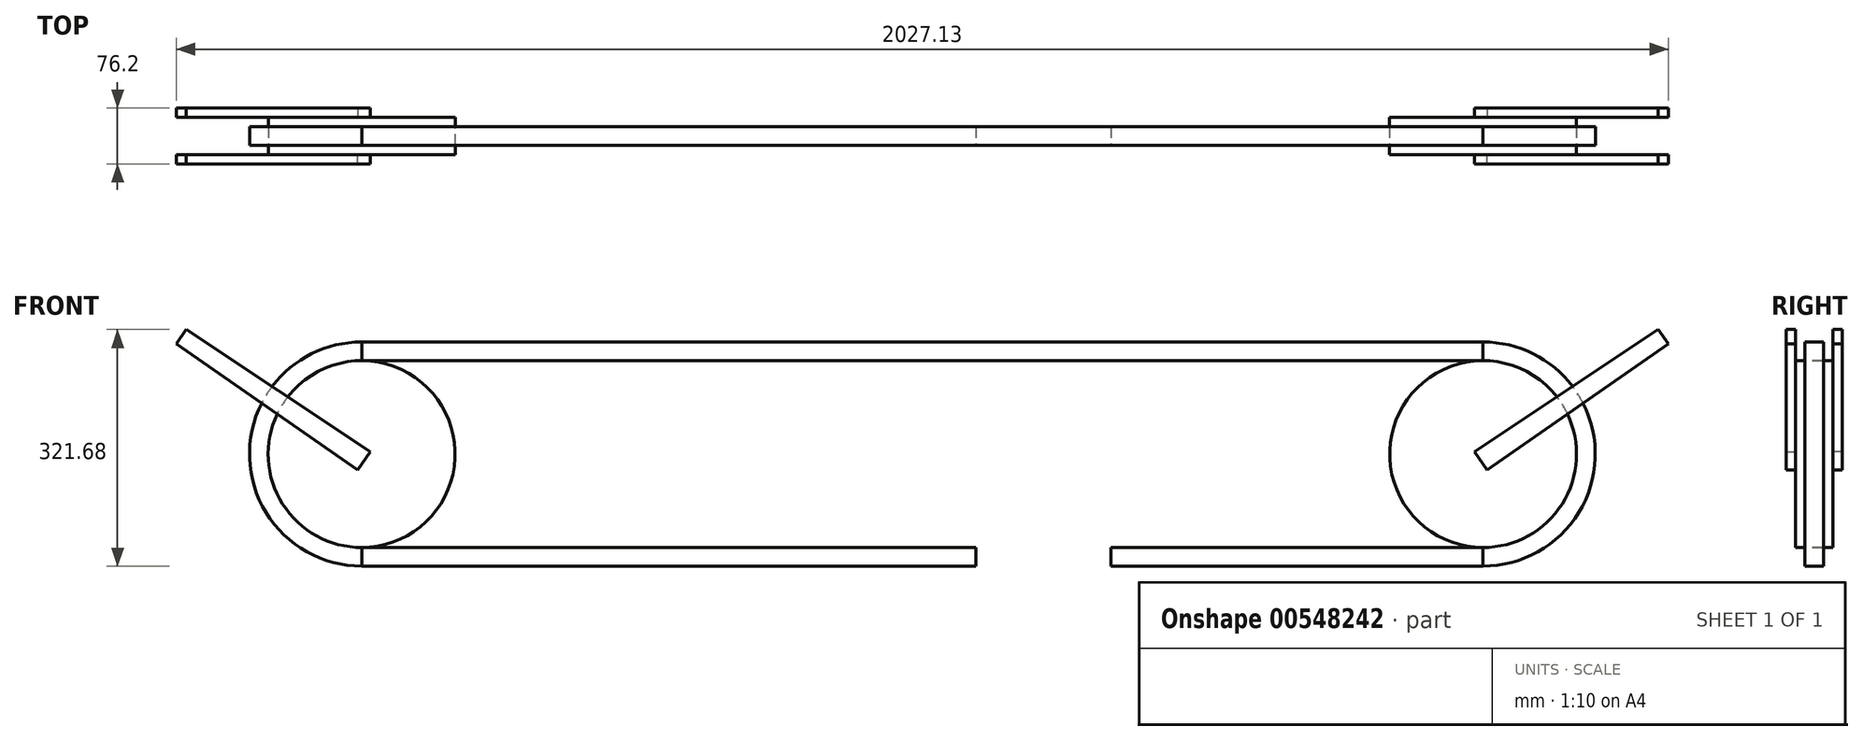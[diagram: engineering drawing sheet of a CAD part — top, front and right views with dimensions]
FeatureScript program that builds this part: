
annotation { "Feature Type Name" : "Feature", "Feature Type Description" : "" }
export const myFeature = defineFeature(function(context is Context, id is Id, definition is map)
    precondition{}
    {
        {
            var Q0;
            Q0=qCreatedBy(makeId("Front.planeOp"),FACE);
            var sketch = newSketch(context, id + "F0", { "sketchPlane" : qUnion([Q0])});
            skLineSegment(sketch, "E0", {"start": v(0, 0) * mm, "end": v(183.8, 0) * mm, "construction": true});
            skLineSegment(sketch, "E1.bottom", {"start": v(0, 0) * mm, "end": v(-834.53, 0) * mm});
            skLineSegment(sketch, "E1.top", {"start": v(0, -25.4) * mm, "end": v(-834.53, -25.4) * mm});
            skLineSegment(sketch, "E1.left", {"start": v(0, 0) * mm, "end": v(0, -25.4) * mm});
            skLineSegment(sketch, "E1.right", {"start": v(-834.53, 0) * mm, "end": v(-834.53, -25.4) * mm});
            skLineSegment(sketch, "E2.bottom", {"start": v(183.8, 0) * mm, "end": v(689.47, 0) * mm});
            skLineSegment(sketch, "E2.top", {"start": v(183.8, -25.4) * mm, "end": v(689.47, -25.4) * mm});
            skLineSegment(sketch, "E2.left", {"start": v(183.8, 0) * mm, "end": v(183.8, -25.4) * mm});
            skLineSegment(sketch, "E2.right", {"start": v(689.47, 0) * mm, "end": v(689.47, -25.4) * mm});
            skLineSegment(sketch, "E3.bottom", {"start": v(-834.53, 254) * mm, "end": v(689.47, 254) * mm});
            skLineSegment(sketch, "E3.top", {"start": v(-834.53, 279.4) * mm, "end": v(689.47, 279.4) * mm});
            skLineSegment(sketch, "E3.left", {"start": v(-834.53, 254) * mm, "end": v(-834.53, 279.4) * mm});
            skLineSegment(sketch, "E3.right", {"start": v(689.47, 254) * mm, "end": v(689.47, 279.4) * mm});
            skSolve(sketch);
        }
        {
            var Q0;
            Q0 = qSketchRegion(id + "F0", true);
            extrude(context, id + "F1", {"entities" : qUnion([Q0]), "endBound" : BoundingType.SYMMETRIC, "oppositeDirection" : true, "depth" : 25.4 * mm, "offsetDistance" : 25.4 * mm});
        }
        {
            var Q0;
            Q0=qCreatedBy(makeId("Front.planeOp"),FACE);
            var sketch = newSketch(context, id + "F2", { "sketchPlane" : qUnion([Q0])});
            skCircle(sketch, "E4", {"center": v(689.47, 127) * mm, "radius": 127 * mm});
            skSolve(sketch);
        }
        {
            var Q0;
            Q0 = qSketchRegion(id + "F2", true);
            extrude(context, id + "F3", {"entities" : qUnion([Q0]), "endBound" : BoundingType.SYMMETRIC, "oppositeDirection" : true, "depth" : 50.8 * mm, "offsetDistance" : 25.4 * mm});
        }
        {
            var Q0;
            Q0=makeQuery(id+"F1.opExtrude","SWEPT_FACE",FACE,{"disambiguationData":[OSD([sQuery(id+"F0.wireOp",EDGE,"E3.right")])]});
            var sketch = newSketch(context, id + "F4", { "sketchPlane" : qUnion([Q0])});
            skLineSegment(sketch, "E5.bottom", {"start": v(-12.7, 254) * mm, "end": v(12.7, 254) * mm});
            skLineSegment(sketch, "E5.top", {"start": v(-12.7, 279.4) * mm, "end": v(12.7, 279.4) * mm});
            skLineSegment(sketch, "E5.left", {"start": v(-12.7, 254) * mm, "end": v(-12.7, 279.4) * mm});
            skLineSegment(sketch, "E5.right", {"start": v(12.7, 254) * mm, "end": v(12.7, 279.4) * mm});
            skLineSegment(sketch, "E6", {"start": v(-32.48, 127) * mm, "end": v(42.83, 127) * mm, "construction": true});
            skSolve(sketch);
        }
        {
            var Q0;
            Q0=makeQuery(id+"F4.imprint","IMPRINT",FACE,{"disambiguationData":[TD([[makeQuery(id+"F4.imprint","IMPRINT",EDGE,{"derivedFrom":sQuery(id+"F4.wireOp",EDGE,"E5.bottom")}),-1.0]])]});
            var Q1;
            Q1=sQuery(id+"F4.wireOp",EDGE,"E6");
            revolve(context, id + "F5", {"entities" : qUnion([Q0]), "axis" : qUnion([Q1]), "revolveType" : RevolveType.ONE_DIRECTION, "angle" : 180 * degree});
        }
        {
            var Q0;
            Q0=makeQuery(id+"F1.opExtrude","SWEPT_FACE",FACE,{"disambiguationData":[OSD([sQuery(id+"F0.wireOp",EDGE,"E3.left")])]});
            cPlane(context, id + "F6", {"entities" : qUnion([Q0]), "cplaneType" : CPlaneType.OFFSET, "offset" : 762 * mm, "oppositeDirection" : true, "width" : 152.4 * mm, "height" : 152.4 * mm});
        }
        {
            var Q0;
            Q0=makeQuery(id+"F3.opExtrude","SWEPT_BODY",BODY,{"disambiguationData":[OSD([sQuery(id+"F2.wireOp",EDGE,"E4")])]});
            var Q1;
            Q1=makeQuery(id+"F5.opRevolve","SWEPT_BODY",BODY,{"disambiguationData":[OSD([sQuery(id+"F4.wireOp",EDGE,"E5.bottom"),sQuery(id+"F4.wireOp",EDGE,"E5.top"),sQuery(id+"F4.wireOp",EDGE,"E5.left"),sQuery(id+"F4.wireOp",EDGE,"E5.right")])]});
            var Q2;
            Q2=qCreatedBy(id+"F6.planeOp",FACE);
            mirror(context, id + "F7", {"entities" : qUnion([Q0, Q1]), "mirrorPlane" : qUnion([Q2])});
        }
        {
            var Q0;
            Q0=makeQuery(id+"F7.opPattern","COPY",FACE,{"derivedFrom":makeQuery(id+"F3.opExtrude","CAP_FACE",FACE,{"disambiguationData":[OSD([sQuery(id+"F2.wireOp",EDGE,"E4")])],"isStart":true}),"instanceName":"1"});
            var sketch = newSketch(context, id + "F8", { "sketchPlane" : qUnion([Q0])});
            skLineSegment(sketch, "E7", {"start": v(-822.71, 130.03) * mm, "end": v(-839.72, 105.58) * mm});
            skLineSegment(sketch, "E8", {"start": v(-839.72, 105.58) * mm, "end": v(-1086.1, 276.98) * mm});
            skLineSegment(sketch, "E9", {"start": v(-1086.1, 276.98) * mm, "end": v(-1072.67, 296.28) * mm});
            skLineSegment(sketch, "E10", {"start": v(-1072.67, 296.28) * mm, "end": v(-822.71, 130.03) * mm});
            skSolve(sketch);
        }
        {
            var Q0;
            {var subQ0=sQuery(id+"F8.wireOp",EDGE,"E9");Q0=makeQuery(id+"F8.imprint","IMPRINT",FACE,{"disambiguationData":[TD([[makeQuery(id+"F8.imprint","IMPRINT",EDGE,{"derivedFrom":subQ0}),-1.0]])]});}
            var Q1;
            {var subQ0=sQuery(id+"F8.wireOp",EDGE,"E7");Q1=makeQuery(id+"F8.imprint","IMPRINT",FACE,{"disambiguationData":[TD([[makeQuery(id+"F8.imprint","IMPRINT",EDGE,{"derivedFrom":subQ0}),-1.0]])]});}
            extrude(context, id + "F9", {"entities" : qUnion([Q0, Q1]), "operationType" : NewBodyOperationType.ADD, "depth" : 12.7 * mm, "offsetDistance" : 25.4 * mm});
        }
        {
            var Q0;
            Q0=makeQuery(id+"F7.opPattern","COPY",BODY,{"derivedFrom":makeQuery(id+"F3.opExtrude","SWEPT_BODY",BODY,{"disambiguationData":[OSD([sQuery(id+"F2.wireOp",EDGE,"E4")])]}),"instanceName":"1"});
            var Q1;
            Q1=qCreatedBy(makeId("Front.planeOp"),FACE);
            mirror(context, id + "F10", {"entities" : qUnion([Q0]), "mirrorPlane" : qUnion([Q1])});
        }
        {
            var Q0;
            Q0=makeQuery(id+"F7.opPattern","COPY",BODY,{"derivedFrom":makeQuery(id+"F3.opExtrude","SWEPT_BODY",BODY,{"disambiguationData":[OSD([sQuery(id+"F2.wireOp",EDGE,"E4")])]}),"instanceName":"1"});
            var Q1;
            Q1=makeQuery(id+"F10.opPattern","COPY",BODY,{"derivedFrom":makeQuery(id+"F7.opPattern","COPY",BODY,{"derivedFrom":makeQuery(id+"F3.opExtrude","SWEPT_BODY",BODY,{"disambiguationData":[OSD([sQuery(id+"F2.wireOp",EDGE,"E4")])]}),"instanceName":"1"}),"instanceName":"1"});
            var Q2;
            Q2=qCreatedBy(id+"F6.planeOp",FACE);
            mirror(context, id + "F11", {"entities" : qUnion([Q0, Q1]), "mirrorPlane" : qUnion([Q2])});
        }
    });
